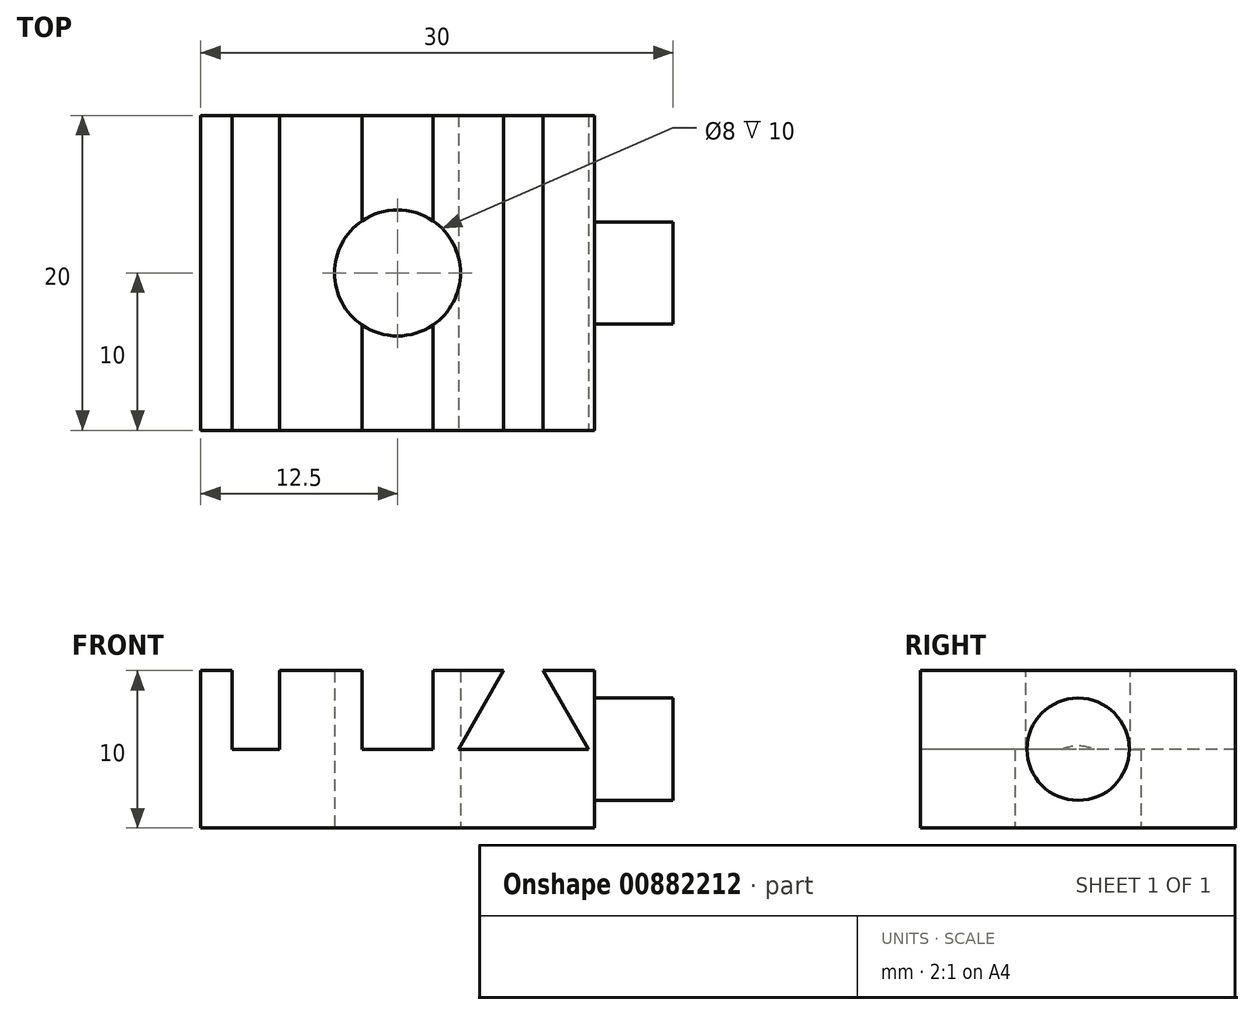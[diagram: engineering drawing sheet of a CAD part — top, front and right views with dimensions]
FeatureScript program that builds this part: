
annotation { "Feature Type Name" : "Feature", "Feature Type Description" : "" }
export const myFeature = defineFeature(function(context is Context, id is Id, definition is map)
    precondition{}
    {
        {
            var Q0;
            Q0=qCreatedBy(makeId("Top.planeOp"),FACE);
            var sketch = newSketch(context, id + "F0", { "sketchPlane" : qUnion([Q0])});
            skLineSegment(sketch, "E0.bottom", {"start": v(-12.5, 10) * mm, "end": v(12.5, 10) * mm});
            skLineSegment(sketch, "E0.top", {"start": v(-12.5, -10) * mm, "end": v(12.5, -10) * mm});
            skLineSegment(sketch, "E0.left", {"start": v(-12.5, 10) * mm, "end": v(-12.5, -10) * mm});
            skLineSegment(sketch, "E0.right", {"start": v(12.5, 10) * mm, "end": v(12.5, -10) * mm});
            skPoint(sketch, "E0.middle", {"position": v(0, 0) * mm});
            skCircle(sketch, "E1", {"center": v(0, 0) * mm, "radius": 4 * mm});
            skSolve(sketch);
        }
        {
            var Q0;
            Q0=makeQuery(id+"F0.imprint","IMPRINT",FACE,{"disambiguationData":[TD([[makeQuery(id+"F0.imprint","IMPRINT",EDGE,{"derivedFrom":sQuery(id+"F0.wireOp",EDGE,"E0.bottom")}),-1.0]])]});
            extrude(context, id + "F1", {"entities" : qUnion([Q0]), "depth" : 10 * mm, "offsetDistance" : 25 * mm});
        }
        {
            var Q0;
            Q0=makeQuery(id+"F1.opExtrude","CAP_FACE",FACE,{"disambiguationData":[OSD([sQuery(id+"F0.wireOp",EDGE,"E0.bottom"),sQuery(id+"F0.wireOp",EDGE,"E0.top"),sQuery(id+"F0.wireOp",EDGE,"E0.left"),sQuery(id+"F0.wireOp",EDGE,"E0.right"),sQuery(id+"F0.wireOp",EDGE,"E1")])],"isStart":false});
            var sketch = newSketch(context, id + "F2", { "sketchPlane" : qUnion([Q0])});
            skLineSegment(sketch, "E2.bottom", {"start": v(-10.5, 10) * mm, "end": v(-7.5, 10) * mm});
            skLineSegment(sketch, "E2.top", {"start": v(-10.5, -10) * mm, "end": v(-7.5, -10) * mm});
            skLineSegment(sketch, "E2.left", {"start": v(-10.5, 10) * mm, "end": v(-10.5, -10) * mm});
            skLineSegment(sketch, "E2.right", {"start": v(-7.5, 10) * mm, "end": v(-7.5, -10) * mm});
            skLineSegment(sketch, "E3", {"start": v(-2.25, 10) * mm, "end": v(-2.25, -10) * mm});
            skLineSegment(sketch, "E4", {"start": v(-2.25, -10) * mm, "end": v(2.25, -10) * mm});
            skLineSegment(sketch, "E5", {"start": v(2.25, -10) * mm, "end": v(2.25, 10) * mm});
            skLineSegment(sketch, "E6", {"start": v(2.25, 10) * mm, "end": v(-2.25, 10) * mm});
            skPoint(sketch, "E7", {"position": v(0, 0) * mm});
            skLineSegment(sketch, "E8", {"start": v(0, 10) * mm, "end": v(0, -10) * mm, "construction": true});
            skSolve(sketch);
        }
        {
            var Q0;
            Q0=makeQuery(id+"F2.imprint","IMPRINT",FACE,{"disambiguationData":[TD([[makeQuery(id+"F2.imprint","IMPRINT",EDGE,{"derivedFrom":sQuery(id+"F2.wireOp",EDGE,"E2.bottom")}),-1.0]])]});
            var Q1;
            {var subQ0=sQuery(id+"F2.wireOp",EDGE,"E6");Q1=makeQuery(id+"F2.imprint","IMPRINT",FACE,{"disambiguationData":[TD([[makeQuery(id+"F2.imprint","IMPRINT",EDGE,{"derivedFrom":subQ0}),-1.0]])]});}
            var Q2;
            {var subQ0=sQuery(id+"F2.wireOp",EDGE,"E4");Q2=makeQuery(id+"F2.imprint","IMPRINT",FACE,{"disambiguationData":[TD([[makeQuery(id+"F2.imprint","IMPRINT",EDGE,{"derivedFrom":subQ0}),1.0]])]});}
            extrude(context, id + "F3", {"entities" : qUnion([Q0, Q1, Q2]), "operationType" : NewBodyOperationType.REMOVE, "flatOperationType" : FlatOperationType.REMOVE, "oppositeDirection" : true, "depth" : 5 * mm, "offsetDistance" : 25 * mm, "domain" : OperationDomain.MODEL});
        }
        {
            var Q0;
            Q0=makeQuery(id+"F1.opExtrude","SWEPT_FACE",FACE,{"disambiguationData":[OSD([sQuery(id+"F0.wireOp",EDGE,"E0.top")])]});
            var sketch = newSketch(context, id + "F4", { "sketchPlane" : qUnion([Q0])});
            skLineSegment(sketch, "E9", {"start": v(6.75, 10) * mm, "end": v(3.86, 5) * mm});
            skLineSegment(sketch, "E10", {"start": v(3.86, 5) * mm, "end": v(12.14, 5) * mm});
            skLineSegment(sketch, "E11", {"start": v(12.14, 5) * mm, "end": v(9.25, 10) * mm});
            skLineSegment(sketch, "E12", {"start": v(9.25, 10) * mm, "end": v(6.75, 10) * mm});
            skLineSegment(sketch, "E13", {"start": v(8, 5) * mm, "end": v(8, 10) * mm, "construction": true});
            skSolve(sketch);
        }
        {
            var Q0;
            Q0=makeQuery(id+"F4.imprint","IMPRINT",FACE,{"disambiguationData":[TD([[makeQuery(id+"F4.imprint","IMPRINT",EDGE,{"derivedFrom":sQuery(id+"F4.wireOp",EDGE,"E9")}),1.0]])]});
            extrude(context, id + "F5", {"entities" : qUnion([Q0]), "operationType" : NewBodyOperationType.REMOVE, "endBound" : BoundingType.THROUGH_ALL, "oppositeDirection" : true, "depth" : 25 * mm, "offsetDistance" : 25 * mm});
        }
        {
            var Q0;
            Q0=makeQuery(id+"F1.opExtrude","SWEPT_FACE",FACE,{"disambiguationData":[OSD([sQuery(id+"F0.wireOp",EDGE,"E0.right")])]});
            var sketch = newSketch(context, id + "F6", { "sketchPlane" : qUnion([Q0])});
            skCircle(sketch, "E14", {"center": v(0, 5) * mm, "radius": 3.25 * mm});
            skPoint(sketch, "E14.centerSnap0", {"position": v(-10, 5) * mm});
            skPoint(sketch, "E14.centerSnap1", {"position": v(0, 10) * mm});
            skSolve(sketch);
        }
        {
            var Q0;
            Q0=makeQuery(id+"F6.imprint","IMPRINT",FACE,{"disambiguationData":[TD([[makeQuery(id+"F6.imprint","IMPRINT",EDGE,{"derivedFrom":sQuery(id+"F6.wireOp",EDGE,"E14")}),1.0]])]});
            extrude(context, id + "F7", {"entities" : qUnion([Q0]), "operationType" : NewBodyOperationType.ADD, "depth" : 5 * mm, "offsetDistance" : 25 * mm});
        }
    });
